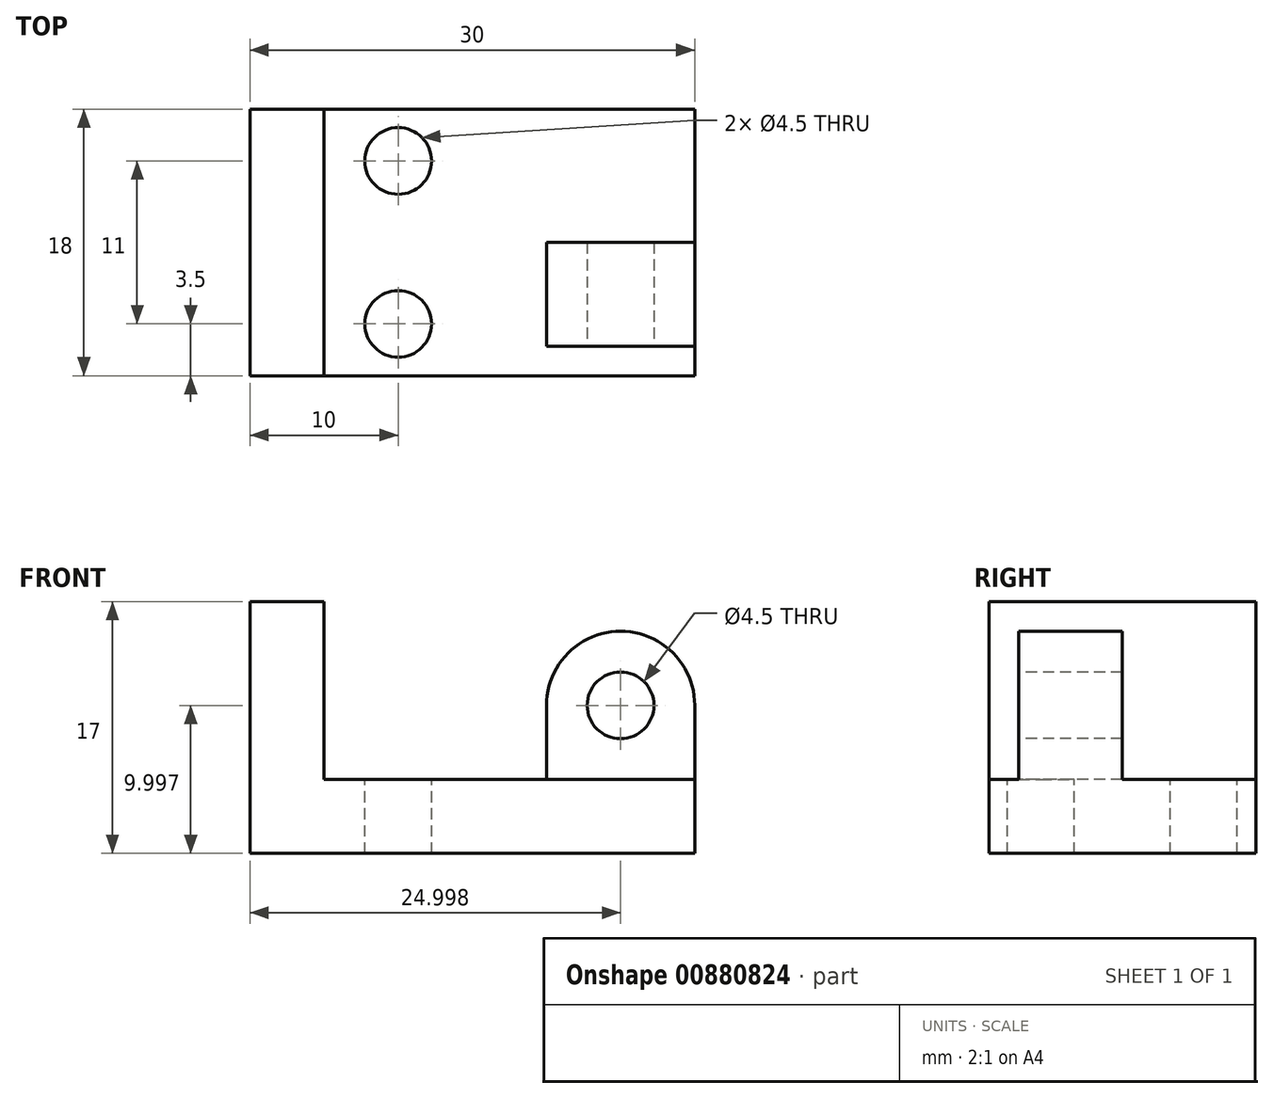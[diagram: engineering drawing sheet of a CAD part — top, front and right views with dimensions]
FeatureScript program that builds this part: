
annotation { "Feature Type Name" : "Feature", "Feature Type Description" : "" }
export const myFeature = defineFeature(function(context is Context, id is Id, definition is map)
    precondition{}
    {
        {
            var Q0;
            Q0=qCreatedBy(makeId("Top.planeOp"),FACE);
            var sketch = newSketch(context, id + "F0", { "sketchPlane" : qUnion([Q0])});
            skLineSegment(sketch, "E0.bottom", {"start": v(15, -9) * mm, "end": v(-15, -9) * mm});
            skLineSegment(sketch, "E0.top", {"start": v(15, 9) * mm, "end": v(-15, 9) * mm});
            skLineSegment(sketch, "E0.left", {"start": v(15, -9) * mm, "end": v(15, 9) * mm});
            skLineSegment(sketch, "E0.right", {"start": v(-15, -9) * mm, "end": v(-15, 9) * mm});
            skPoint(sketch, "E0.middle", {"position": v(0, 0) * mm});
            skSolve(sketch);
        }
        {
            var Q0;
            Q0=qSketchRegion(id+"F0",true);
            extrude(context, id + "F1", {"entities" : qUnion([Q0]), "depth" : 5 * mm, "offsetDistance" : 25 * mm});
        }
        {
            var Q0;
            Q0=makeQuery(id+"F1.opExtrude","CAP_FACE",FACE,{"disambiguationData":[OSD([sQuery(id+"F0.wireOp",EDGE,"E0.bottom"),sQuery(id+"F0.wireOp",EDGE,"E0.top"),sQuery(id+"F0.wireOp",EDGE,"E0.left"),sQuery(id+"F0.wireOp",EDGE,"E0.right")])],"isStart":false});
            var sketch = newSketch(context, id + "F2", { "sketchPlane" : qUnion([Q0])});
            skCircle(sketch, "E1", {"center": v(-5, 5.5) * mm, "radius": 2.25 * mm});
            skCircle(sketch, "E2.MirrorC", {"center": v(-5, -5.5) * mm, "radius": 2.25 * mm});
            skSolve(sketch);
        }
        {
            var Q0;
            Q0=qSketchRegion(id+"F2",true);
            extrude(context, id + "F3", {"entities" : qUnion([Q0]), "operationType" : NewBodyOperationType.REMOVE, "endBound" : BoundingType.UP_TO_NEXT, "oppositeDirection" : true, "depth" : 25 * mm, "offsetDistance" : 25 * mm});
        }
        {
            var Q0;
            Q0=makeQuery(id+"F1.opExtrude","SWEPT_FACE",FACE,{"disambiguationData":[OSD([sQuery(id+"F0.wireOp",EDGE,"E0.bottom")])]});
            var sketch = newSketch(context, id + "F4", { "sketchPlane" : qUnion([Q0])});
            skArc(sketch, "E3", {"start": v(15, 10) * mm, "mid": v(10, 15) * mm, "end": v(5, 10) * mm});
            skLineSegment(sketch, "E4", {"start": v(15, 5) * mm, "end": v(15, 10) * mm});
            skLineSegment(sketch, "E5", {"start": v(5, 10) * mm, "end": v(5, 5) * mm});
            skLineSegment(sketch, "E6", {"start": v(5, 5) * mm, "end": v(15, 5) * mm});
            skSolve(sketch);
        }
        {
            var Q0;
            Q0=qSketchRegion(id+"F4",true);
            extrude(context, id + "F5", {"entities" : qUnion([Q0]), "operationType" : NewBodyOperationType.ADD, "oppositeDirection" : true, "depth" : 9 * mm, "offsetDistance" : 25 * mm, "hasSecondDirection" : true, "secondDirectionOppositeDirection" : true, "secondDirectionDepth" : 2 * mm});
        }
        {
            var Q0;
            Q0=makeQuery(id+"F5.opExtrude","CAP_FACE",FACE,{"disambiguationData":[OSD([sQuery(id+"F4.wireOp",EDGE,"E3"),sQuery(id+"F4.wireOp",EDGE,"E4"),sQuery(id+"F4.wireOp",EDGE,"E5"),sQuery(id+"F4.wireOp",EDGE,"E6")])],"isStart":true});
            var sketch = newSketch(context, id + "F6", { "sketchPlane" : qUnion([Q0])});
            skCircle(sketch, "E7", {"center": v(10, 10) * mm, "radius": 2.25 * mm});
            skLineSegment(sketch, "E8", {"start": v(10, 15) * mm, "end": v(10, 1.72) * mm, "construction": true});
            skLineSegment(sketch, "E9", {"start": v(5, 10) * mm, "end": v(15.94, 10) * mm});
            skSolve(sketch);
        }
        {
            var Q0;
            Q0=qSketchRegion(id+"F6",true);
            extrude(context, id + "F7", {"entities" : qUnion([Q0]), "operationType" : NewBodyOperationType.REMOVE, "endBound" : BoundingType.UP_TO_NEXT, "oppositeDirection" : true, "depth" : 25 * mm, "offsetDistance" : 25 * mm});
        }
        {
            var Q0;
            Q0=makeQuery(id+"F1.opExtrude","SWEPT_FACE",FACE,{"disambiguationData":[OSD([sQuery(id+"F0.wireOp",EDGE,"E0.bottom")])]});
            var sketch = newSketch(context, id + "F8", { "sketchPlane" : qUnion([Q0])});
            skLineSegment(sketch, "E10.bottom", {"start": v(-15, 17) * mm, "end": v(-10, 17) * mm});
            skLineSegment(sketch, "E10.top", {"start": v(-15, 5) * mm, "end": v(-10, 5) * mm});
            skLineSegment(sketch, "E10.left", {"start": v(-15, 17) * mm, "end": v(-15, 5) * mm});
            skLineSegment(sketch, "E10.right", {"start": v(-10, 17) * mm, "end": v(-10, 5) * mm});
            skSolve(sketch);
        }
        {
            var Q0;
            Q0 = qSketchRegion(id + "F8", true);
            extrude(context, id + "F9", {"entities" : qUnion([Q0]), "operationType" : NewBodyOperationType.ADD, "oppositeDirection" : true, "depth" : 18 * mm, "offsetDistance" : 25 * mm});
        }
    });
